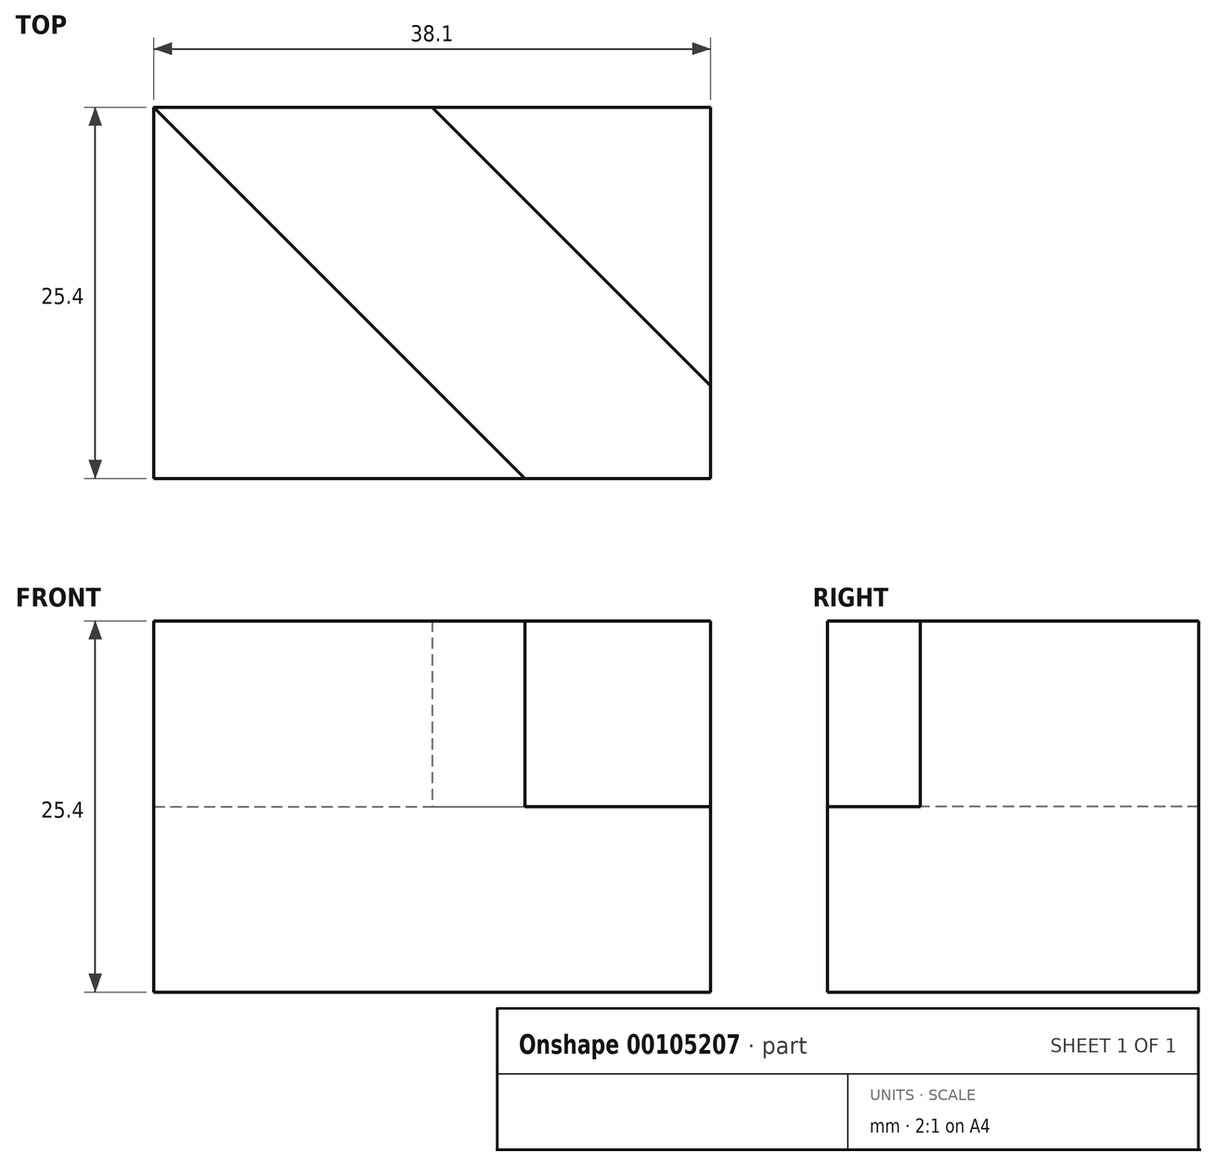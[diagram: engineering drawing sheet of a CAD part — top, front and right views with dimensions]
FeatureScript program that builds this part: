
annotation { "Feature Type Name" : "Feature", "Feature Type Description" : "" }
export const myFeature = defineFeature(function(context is Context, id is Id, definition is map)
    precondition{}
    {
        {
            var Q0;
            Q0=qCreatedBy(makeId("Top.planeOp"),FACE);
            var sketch = newSketch(context, id + "F0", { "sketchPlane" : qUnion([Q0])});
            skLineSegment(sketch, "E0", {"start": v(0, 0) * mm, "end": v(0, 25.4) * mm});
            skLineSegment(sketch, "E1", {"start": v(0, 25.4) * mm, "end": v(38.1, 25.4) * mm});
            skLineSegment(sketch, "E2", {"start": v(38.1, 25.4) * mm, "end": v(38.1, 0) * mm});
            skLineSegment(sketch, "E3", {"start": v(38.1, 0) * mm, "end": v(0, 0) * mm});
            skLineSegment(sketch, "E4", {"start": v(0, 25.4) * mm, "end": v(25.4, 0) * mm});
            skLineSegment(sketch, "E5", {"start": v(19.05, 25.4) * mm, "end": v(38.1, 6.35) * mm});
            skLineSegment(sketch, "E6", {"start": v(38.1, 6.35) * mm, "end": v(38.1, 0) * mm});
            skLineSegment(sketch, "E7", {"start": v(25.4, 0) * mm, "end": v(38.1, 0) * mm});
            skLineSegment(sketch, "E8", {"start": v(19.05, 25.4) * mm, "end": v(0, 25.4) * mm});
            skSolve(sketch);
        }
        {
            var Q0;
            Q0=makeQuery(id+"F0.imprint","IMPRINT",FACE,{"disambiguationData":[TD([[makeQuery(id+"F0.imprint","IMPRINT",EDGE,{"derivedFrom":sQuery(id+"F0.wireOp",EDGE,"E0")}),-1.0]])]});
            extrude(context, id + "F1", {"entities" : qUnion([Q0]), "depth" : 25.4 * mm});
        }
        {
            var Q0;
            Q0=makeQuery(id+"F0.imprint","IMPRINT",FACE,{"disambiguationData":[TD([[makeQuery(id+"F0.imprint","IMPRINT",EDGE,{"derivedFrom":sQuery(id+"F0.wireOp",EDGE,"E4")}),1.0]])]});
            extrude(context, id + "F2", {"entities" : qUnion([Q0]), "operationType" : NewBodyOperationType.ADD, "depth" : 12.7 * mm});
        }
        {
            var Q0;
            Q0=makeQuery(id+"F0.imprint","IMPRINT",FACE,{"disambiguationData":[TD([[makeQuery(id+"F0.imprint","IMPRINT",EDGE,{"derivedFrom":sQuery(id+"F0.wireOp",EDGE,"E1")}),-1.0]])]});
            extrude(context, id + "F3", {"entities" : qUnion([Q0]), "operationType" : NewBodyOperationType.ADD, "depth" : 25.4 * mm});
        }
    });
